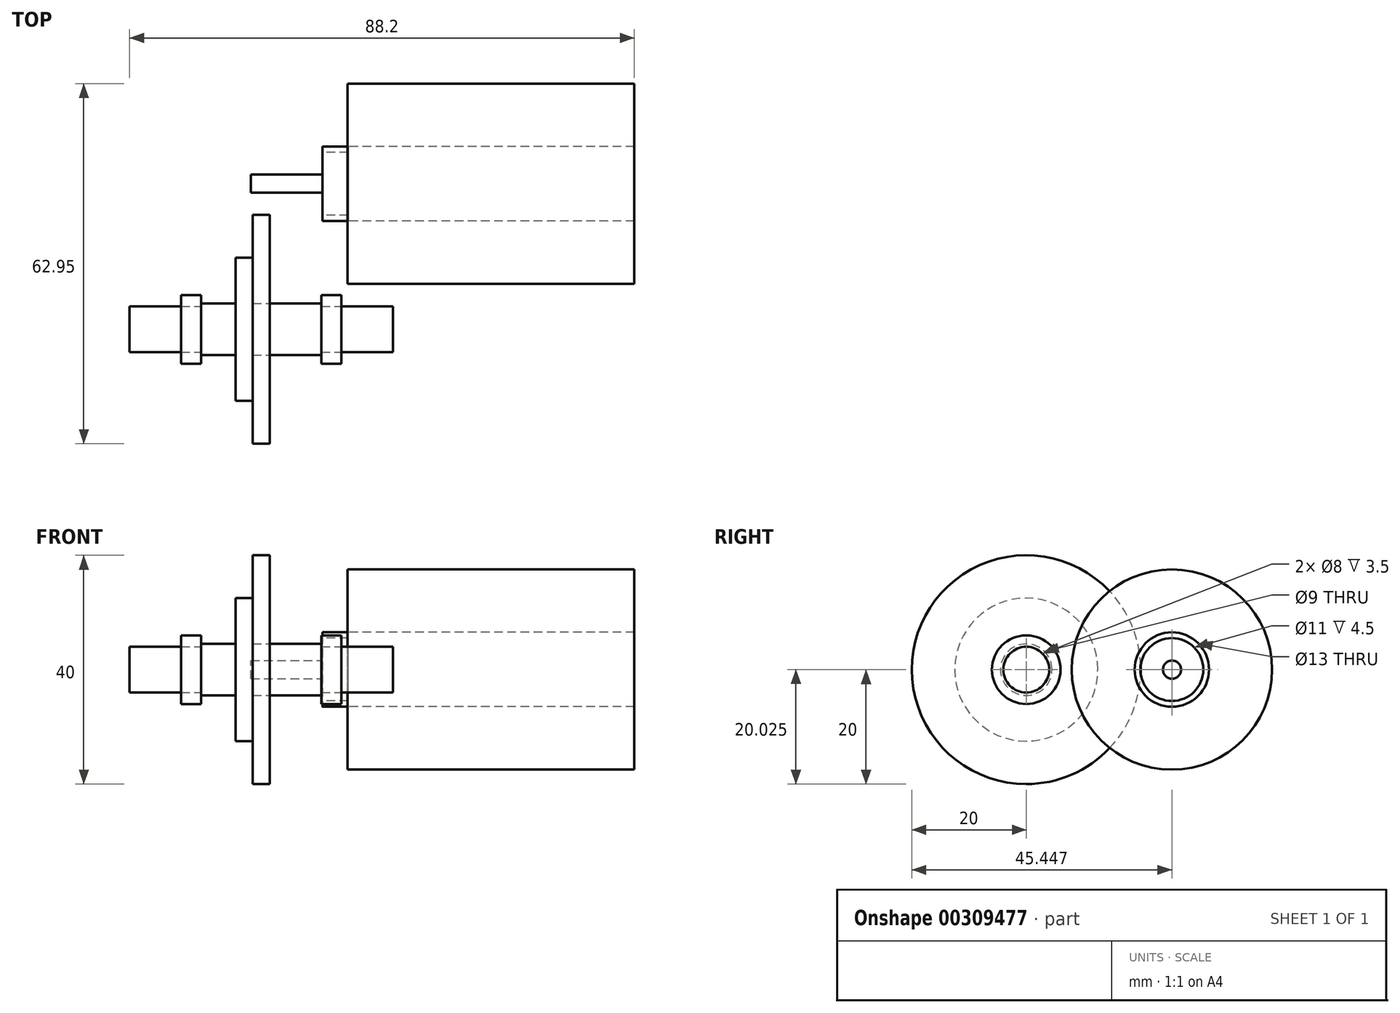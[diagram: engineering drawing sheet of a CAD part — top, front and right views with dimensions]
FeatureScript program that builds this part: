
annotation { "Feature Type Name" : "Feature", "Feature Type Description" : "" }
export const myFeature = defineFeature(function(context is Context, id is Id, definition is map)
    precondition{}
    {
        {
            var Q0;
            Q0=qCreatedBy(makeId("Top.planeOp"),FACE);
            var sketch = newSketch(context, id + "F0", { "sketchPlane" : qUnion([Q0])});
            skLineSegment(sketch, "E0.bottom", {"start": v(20, 4) * mm, "end": v(-20, 4) * mm});
            skLineSegment(sketch, "E0.top", {"start": v(20, -4) * mm, "end": v(-20, -4) * mm});
            skLineSegment(sketch, "E0.left", {"start": v(20, 4) * mm, "end": v(20, -4) * mm});
            skLineSegment(sketch, "E0.right", {"start": v(-20, 4) * mm, "end": v(-20, -4) * mm});
            skPoint(sketch, "E0.middle", {"position": v(0, 0) * mm});
            skLineSegment(sketch, "E1.bottom", {"start": v(-1.5, 20) * mm, "end": v(1.5, 20) * mm});
            skLineSegment(sketch, "E1.top", {"start": v(-1.5, -20) * mm, "end": v(1.5, -20) * mm});
            skLineSegment(sketch, "E1.left", {"start": v(-1.5, 20) * mm, "end": v(-1.5, -20) * mm});
            skLineSegment(sketch, "E1.right", {"start": v(1.5, 20) * mm, "end": v(1.5, -20) * mm});
            skLineSegment(sketch, "E2.bottom", {"start": v(20, 4) * mm, "end": v(14, 4) * mm});
            skLineSegment(sketch, "E2.top", {"start": v(20, -4) * mm, "end": v(14, -4) * mm});
            skLineSegment(sketch, "E2.right", {"start": v(14, 4) * mm, "end": v(14, -4) * mm});
            skLineSegment(sketch, "E3.bottom", {"start": v(-20, 4) * mm, "end": v(-14, 4) * mm});
            skLineSegment(sketch, "E3.top", {"start": v(-20, -4) * mm, "end": v(-14, -4) * mm});
            skLineSegment(sketch, "E3.right", {"start": v(-14, 4) * mm, "end": v(-14, -4) * mm});
            skLineSegment(sketch, "E4.bottom", {"start": v(-1.5, 12.5) * mm, "end": v(-4.5, 12.5) * mm});
            skLineSegment(sketch, "E4.top", {"start": v(-1.5, -12.5) * mm, "end": v(-4.5, -12.5) * mm});
            skLineSegment(sketch, "E4.left", {"start": v(-1.5, 12.5) * mm, "end": v(-1.5, -12.5) * mm});
            skLineSegment(sketch, "E4.right", {"start": v(-4.5, 12.5) * mm, "end": v(-4.5, -12.5) * mm});
            skPoint(sketch, "E4.middle", {"position": v(-3, 0) * mm});
            skLineSegment(sketch, "E5.top", {"start": v(-14, 6) * mm, "end": v(-10.5, 6) * mm});
            skLineSegment(sketch, "E5.left", {"start": v(-14, 0) * mm, "end": v(-14, 6) * mm});
            skLineSegment(sketch, "E5.right", {"start": v(-10.5, 0) * mm, "end": v(-10.5, 6) * mm});
            skLineSegment(sketch, "E6.MirrorCS", {"start": v(-14, 12) * mm, "end": v(-14, 6) * mm});
            skLineSegment(sketch, "E7.MirrorCS", {"start": v(-10.5, 12) * mm, "end": v(-10.5, 6) * mm});
            skLineSegment(sketch, "E8.top", {"start": v(-14, -6) * mm, "end": v(-10.5, -6) * mm});
            skLineSegment(sketch, "E8.left", {"start": v(-14, 6) * mm, "end": v(-14, -6) * mm});
            skLineSegment(sketch, "E8.right", {"start": v(-10.5, 6) * mm, "end": v(-10.5, -6) * mm});
            skLineSegment(sketch, "E9.MirrorCS", {"start": v(14, 6) * mm, "end": v(14, -6) * mm});
            skLineSegment(sketch, "E10.MirrorCS", {"start": v(10.5, 6) * mm, "end": v(10.5, -6) * mm});
            skLineSegment(sketch, "E11.MirrorCS", {"start": v(14, 6) * mm, "end": v(10.5, 6) * mm});
            skLineSegment(sketch, "E12.MirrorCS", {"start": v(14, -6) * mm, "end": v(10.5, -6) * mm});
            skLineSegment(sketch, "E13.bottom", {"start": v(10.5, 4.5) * mm, "end": v(-10.5, 4.5) * mm});
            skLineSegment(sketch, "E13.top", {"start": v(10.5, -4.5) * mm, "end": v(-10.5, -4.5) * mm});
            skLineSegment(sketch, "E13.left", {"start": v(10.5, 4.5) * mm, "end": v(10.5, -4.5) * mm});
            skLineSegment(sketch, "E13.right", {"start": v(-10.5, 4.5) * mm, "end": v(-10.5, -4.5) * mm});
            skLineSegment(sketch, "E14", {"start": v(30.83, 0) * mm, "end": v(-35.48, 0) * mm});
            skSolve(sketch);
        }
        {
            var Q0;
            {var subQ0=sQuery(id+"F0.wireOp",EDGE,"E0.right");var subQ1=sQuery(id+"F0.wireOp",EDGE,"E0.bottom");var subQ2=makeQuery(id+"F0.imprint","INTERSECT",VERTEX,{"derivedFrom":[subQ1,subQ0]});Q0=makeQuery(id+"F0.imprint","IMPRINT",FACE,{"disambiguationData":[TD([[makeQuery(id+"F0.imprint","IMPRINT",EDGE,{"disambiguationData":[TD([[subQ2,-1.0]])],"derivedFrom":subQ0}),1.0]])]});}
            var Q1;
            {var subQ1=sQuery(id+"F0.wireOp",EDGE,"E0.bottom");var subQ3=sQuery(id+"F0.wireOp",EDGE,"E5.right");var subQ4=makeQuery(id+"F0.imprint","INTERSECT",VERTEX,{"derivedFrom":[subQ1,subQ3]});Q1=makeQuery(id+"F0.imprint","IMPRINT",FACE,{"disambiguationData":[TD([[makeQuery(id+"F0.imprint","IMPRINT",EDGE,{"disambiguationData":[TD([[subQ4,-1.0]])],"derivedFrom":subQ1}),1.0]])]});}
            var Q2;
            {var subQ0=sQuery(id+"F0.wireOp",EDGE,"E5.right");var subQ1=sQuery(id+"F0.wireOp",EDGE,"E0.bottom");var subQ2=makeQuery(id+"F0.imprint","INTERSECT",VERTEX,{"derivedFrom":[subQ1,subQ0]});Q2=makeQuery(id+"F0.imprint","IMPRINT",FACE,{"disambiguationData":[TD([[makeQuery(id+"F0.imprint","IMPRINT",EDGE,{"disambiguationData":[TD([[subQ2,1.0]])],"derivedFrom":subQ1}),-1.0]])]});}
            var Q3;
            {var subQ0=sQuery(id+"F0.wireOp",EDGE,"E1.left");var subQ1=sQuery(id+"F0.wireOp",EDGE,"E0.bottom");var subQ2=makeQuery(id+"F0.imprint","INTERSECT",VERTEX,{"derivedFrom":[subQ1,subQ0]});Q3=makeQuery(id+"F0.imprint","IMPRINT",FACE,{"disambiguationData":[TD([[makeQuery(id+"F0.imprint","IMPRINT",EDGE,{"disambiguationData":[TD([[subQ2,-1.0]])],"derivedFrom":subQ1}),-1.0]])]});}
            var Q4;
            {var subQ0=sQuery(id+"F0.wireOp",EDGE,"E4.bottom");Q4=makeQuery(id+"F0.imprint","IMPRINT",FACE,{"disambiguationData":[TD([[makeQuery(id+"F0.imprint","IMPRINT",EDGE,{"derivedFrom":subQ0}),1.0]])]});}
            var Q5;
            {var subQ0=sQuery(id+"F0.wireOp",EDGE,"E1.left");var subQ1=sQuery(id+"F0.wireOp",EDGE,"E0.bottom");var subQ2=makeQuery(id+"F0.imprint","INTERSECT",VERTEX,{"derivedFrom":[subQ1,subQ0]});Q5=makeQuery(id+"F0.imprint","IMPRINT",FACE,{"disambiguationData":[TD([[makeQuery(id+"F0.imprint","IMPRINT",EDGE,{"disambiguationData":[TD([[subQ2,-1.0]])],"derivedFrom":subQ1}),1.0]])]});}
            var Q6;
            {var subQ0=sQuery(id+"F0.wireOp",EDGE,"E5.right");var subQ1=sQuery(id+"F0.wireOp",EDGE,"E0.bottom");var subQ2=makeQuery(id+"F0.imprint","INTERSECT",VERTEX,{"derivedFrom":[subQ1,subQ0]});Q6=makeQuery(id+"F0.imprint","IMPRINT",FACE,{"disambiguationData":[TD([[makeQuery(id+"F0.imprint","IMPRINT",EDGE,{"disambiguationData":[TD([[subQ2,1.0]])],"derivedFrom":subQ1}),1.0]])]});}
            var Q7;
            {var subQ0=sQuery(id+"F0.wireOp",EDGE,"E1.left");var subQ1=sQuery(id+"F0.wireOp",EDGE,"E0.bottom");var subQ2=makeQuery(id+"F0.imprint","INTERSECT",VERTEX,{"derivedFrom":[subQ1,subQ0]});Q7=makeQuery(id+"F0.imprint","IMPRINT",FACE,{"disambiguationData":[TD([[makeQuery(id+"F0.imprint","IMPRINT",EDGE,{"disambiguationData":[TD([[subQ2,1.0]])],"derivedFrom":subQ1}),1.0]])]});}
            var Q8;
            {var subQ0=sQuery(id+"F0.wireOp",EDGE,"E1.left");var subQ1=sQuery(id+"F0.wireOp",EDGE,"E0.bottom");var subQ2=makeQuery(id+"F0.imprint","INTERSECT",VERTEX,{"derivedFrom":[subQ1,subQ0]});Q8=makeQuery(id+"F0.imprint","IMPRINT",FACE,{"disambiguationData":[TD([[makeQuery(id+"F0.imprint","IMPRINT",EDGE,{"disambiguationData":[TD([[subQ2,1.0]])],"derivedFrom":subQ1}),-1.0]])]});}
            var Q9;
            {var subQ0=sQuery(id+"F0.wireOp",EDGE,"E10.MirrorCS");var subQ1=sQuery(id+"F0.wireOp",EDGE,"E0.bottom");var subQ2=makeQuery(id+"F0.imprint","INTERSECT",VERTEX,{"derivedFrom":[subQ1,subQ0]});Q9=makeQuery(id+"F0.imprint","IMPRINT",FACE,{"disambiguationData":[TD([[makeQuery(id+"F0.imprint","IMPRINT",EDGE,{"disambiguationData":[TD([[subQ2,-1.0]])],"derivedFrom":subQ1}),1.0]])]});}
            var Q10;
            {var subQ0=sQuery(id+"F0.wireOp",EDGE,"E10.MirrorCS");var subQ1=sQuery(id+"F0.wireOp",EDGE,"E0.bottom");var subQ2=makeQuery(id+"F0.imprint","INTERSECT",VERTEX,{"derivedFrom":[subQ1,subQ0]});Q10=makeQuery(id+"F0.imprint","IMPRINT",FACE,{"disambiguationData":[TD([[makeQuery(id+"F0.imprint","IMPRINT",EDGE,{"disambiguationData":[TD([[subQ2,-1.0]])],"derivedFrom":subQ1}),-1.0]])]});}
            var Q11;
            {var subQ0=sQuery(id+"F0.wireOp",EDGE,"E10.MirrorCS");var subQ1=sQuery(id+"F0.wireOp",EDGE,"E0.bottom");var subQ2=makeQuery(id+"F0.imprint","INTERSECT",VERTEX,{"derivedFrom":[subQ1,subQ0]});Q11=makeQuery(id+"F0.imprint","IMPRINT",FACE,{"disambiguationData":[TD([[makeQuery(id+"F0.imprint","IMPRINT",EDGE,{"disambiguationData":[TD([[subQ2,-1.0]])],"derivedFrom":subQ0}),1.0]])]});}
            var Q12;
            {var subQ0=sQuery(id+"F0.wireOp",EDGE,"E0.left");var subQ5=sQuery(id+"F0.wireOp",EDGE,"E14");var subQ6=makeQuery(id+"F0.imprint","INTERSECT",VERTEX,{"derivedFrom":[subQ0,subQ5]});Q12=makeQuery(id+"F0.imprint","IMPRINT",FACE,{"disambiguationData":[TD([[makeQuery(id+"F0.imprint","IMPRINT",EDGE,{"disambiguationData":[TD([[subQ6,1.0]])],"derivedFrom":subQ0}),-1.0]])]});}
            var Q13;
            Q13=sQuery(id+"F0.wireOp",EDGE,"E14");
            revolve(context, id + "F1", {"surfaceOperationType" : NewSurfaceOperationType.NEW, "entities" : qUnion([Q0, Q1, Q2, Q3, Q4, Q5, Q6, Q7, Q8, Q9, Q10, Q11, Q12]), "axis" : qUnion([Q13]), "revolveType" : RevolveType.FULL});
        }
        {
            var Q0;
            Q0=makeQuery(id+"F1.opRevolve","SWEPT_FACE",FACE,{"disambiguationData":[OSD([sQuery(id+"F0.wireOp",EDGE,"E0.left")])]});
            extrude(context, id + "F2", {"entities" : qUnion([Q0]), "operationType" : NewBodyOperationType.ADD, "depth" : 3 * mm, "offsetDistance" : 25 * mm});
        }
        {
            var Q0;
            Q0=makeQuery(id+"F1.opRevolve","SWEPT_FACE",FACE,{"disambiguationData":[OSD([sQuery(id+"F0.wireOp",EDGE,"E0.right")])]});
            extrude(context, id + "F3", {"entities" : qUnion([Q0]), "operationType" : NewBodyOperationType.ADD, "depth" : 3 * mm, "offsetDistance" : 25 * mm});
        }
        {
            var Q0;
            {var subQ1=sQuery(id+"F0.wireOp",EDGE,"E5.top");Q0=makeQuery(id+"F0.imprint","IMPRINT",FACE,{"disambiguationData":[TD([[makeQuery(id+"F0.imprint","IMPRINT",EDGE,{"derivedFrom":subQ1}),-1.0]])]});}
            var Q1;
            {var subQ4=sQuery(id+"F0.wireOp",EDGE,"E11.MirrorCS");Q1=makeQuery(id+"F0.imprint","IMPRINT",FACE,{"disambiguationData":[TD([[makeQuery(id+"F0.imprint","IMPRINT",EDGE,{"derivedFrom":subQ4}),1.0]])]});}
            var Q2;
            Q2=sQuery(id+"F0.wireOp",EDGE,"E14");
            revolve(context, id + "F4", {"surfaceOperationType" : NewSurfaceOperationType.NEW, "entities" : qUnion([Q0, Q1]), "axis" : qUnion([Q2]), "revolveType" : RevolveType.FULL});
        }
        {
            var Q0;
            {var subQ1=sQuery(id+"F0.wireOp",EDGE,"E1.top");Q0=makeQuery(id+"F0.imprint","IMPRINT",FACE,{"disambiguationData":[TD([[makeQuery(id+"F0.imprint","IMPRINT",EDGE,{"derivedFrom":subQ1}),1.0]])]});}
            var Q1;
            Q1=sQuery(id+"F0.wireOp",EDGE,"E14");
            revolve(context, id + "F5", {"surfaceOperationType" : NewSurfaceOperationType.NEW, "entities" : qUnion([Q0]), "axis" : qUnion([Q1]), "revolveType" : RevolveType.FULL});
        }
        {
            var Q0;
            Q0=qCreatedBy(makeId("Right.planeOp"),FACE);
            var sketch = newSketch(context, id + "F6", { "sketchPlane" : qUnion([Q0])});
            skLineSegment(sketch, "E15.bottom", {"start": v(40, 25) * mm, "end": v(-40, 25) * mm});
            skLineSegment(sketch, "E15.top", {"start": v(40, -25) * mm, "end": v(-40, -25) * mm});
            skLineSegment(sketch, "E15.left", {"start": v(40, 25) * mm, "end": v(40, -25) * mm});
            skLineSegment(sketch, "E15.right", {"start": v(-40, 25) * mm, "end": v(-40, -25) * mm});
            skPoint(sketch, "E15.middle", {"position": v(0, 0) * mm});
            skCircle(sketch, "E16", {"center": v(25.45, 0.03) * mm, "radius": 5.5 * mm});
            skPoint(sketch, "E16.first.point", {"position": v(19.95, 0) * mm});
            skPoint(sketch, "E16.second.point", {"position": v(30.95, 0) * mm});
            skPoint(sketch, "E16.third.point", {"position": v(27.42, -5.1) * mm});
            skCircle(sketch, "E17", {"center": v(25.45, 0.03) * mm, "radius": 17.5 * mm});
            skCircle(sketch, "E18", {"center": v(25.45, 0.03) * mm, "radius": 12.5 * mm});
            skCircle(sketch, "E19", {"center": v(25.45, 0.03) * mm, "radius": 6.5 * mm});
            skSolve(sketch);
        }
        {
            var Q0;
            Q0=makeQuery(id+"F6.imprint","IMPRINT",FACE,{"disambiguationData":[TD([[makeQuery(id+"F6.imprint","IMPRINT",EDGE,{"derivedFrom":sQuery(id+"F6.wireOp",EDGE,"E16")}),-1.0]])]});
            extrude(context, id + "F7", {"entities" : qUnion([Q0]), "depth" : 4.5 * mm, "offsetDistance" : 25 * mm});
        }
        {
            var Q0;
            Q0=makeQuery(id+"F6.imprint","IMPRINT",FACE,{"disambiguationData":[TD([[makeQuery(id+"F6.imprint","IMPRINT",EDGE,{"derivedFrom":sQuery(id+"F6.wireOp",EDGE,"E18")}),1.0]])]});
            var Q1;
            Q1=makeQuery(id+"F6.imprint","IMPRINT",FACE,{"disambiguationData":[TD([[makeQuery(id+"F6.imprint","IMPRINT",EDGE,{"derivedFrom":sQuery(id+"F6.wireOp",EDGE,"E18")}),-1.0]])]});
            var Q2;
            {var subQ0=sQuery(id+"F6.wireOp",EDGE,"E17");var subQ1=sQuery(id+"F6.wireOp",EDGE,"E15.left");var subQ2=makeQuery(id+"F6.imprint","INTERSECT",VERTEX,{"disambiguationData":[OD(0.0)],"derivedFrom":[subQ1,subQ0]});Q2=makeQuery(id+"F6.imprint","IMPRINT",FACE,{"disambiguationData":[TD([[makeQuery(id+"F6.imprint","IMPRINT",EDGE,{"disambiguationData":[TD([[subQ2,-1.0]])],"derivedFrom":subQ1}),1.0]])]});}
            extrude(context, id + "F8", {"entities" : qUnion([Q0, Q1, Q2]), "depth" : 54.5 * mm, "offsetDistance" : 25 * mm, "hasSecondDirection" : true, "secondDirectionOppositeDirection" : false, "secondDirectionDepth" : 4.4 * mm});
        }
        {
            var Q0;
            {var subQ1=sQuery(id+"F6.wireOp",EDGE,"E15.bottom");Q0=makeQuery(id+"F6.imprint","IMPRINT",FACE,{"disambiguationData":[TD([[makeQuery(id+"F6.imprint","IMPRINT",EDGE,{"derivedFrom":subQ1}),1.0]])]});}
            var sketch = newSketch(context, id + "F9", { "sketchPlane" : qUnion([Q0])});
            skCircle(sketch, "E20", {"center": v(25.47, 0) * mm, "radius": 1.59 * mm});
            skSolve(sketch);
        }
        {
            var Q0;
            Q0 = qSketchRegion(id + "F9", true);
            extrude(context, id + "F10", {"entities" : qUnion([Q0]), "oppositeDirection" : true, "depth" : 12.5 * mm, "offsetDistance" : 25 * mm});
        }
        {
            var Q0;
            Q0=makeQuery(id+"F8.opExtrude","SWEPT_BODY",BODY,{"disambiguationData":[OSD([sQuery(id+"F6.wireOp",EDGE,"E17"),sQuery(id+"F6.wireOp",EDGE,"E19")])]});
            var Q1;
            Q1=makeQuery(id+"F7.opExtrude","SWEPT_BODY",BODY,{"disambiguationData":[OSD([sQuery(id+"F6.wireOp",EDGE,"E16"),sQuery(id+"F6.wireOp",EDGE,"E19")])]});
            var Q2;
            Q2=makeQuery(id+"F10.opExtrude","SWEPT_BODY",BODY,{"disambiguationData":[OSD([sQuery(id+"F9.wireOp",EDGE,"E20")])]});
            transform(context, id + "F11", {"entities" : qUnion([Q0, Q1, Q2]), "transformType" : TransformType.TRANSLATION_3D, "dx" : 10.7 * mm, "dy" : 0 * mm, "dz" : 0 * mm, "makeCopy" : false});
        }
    });
